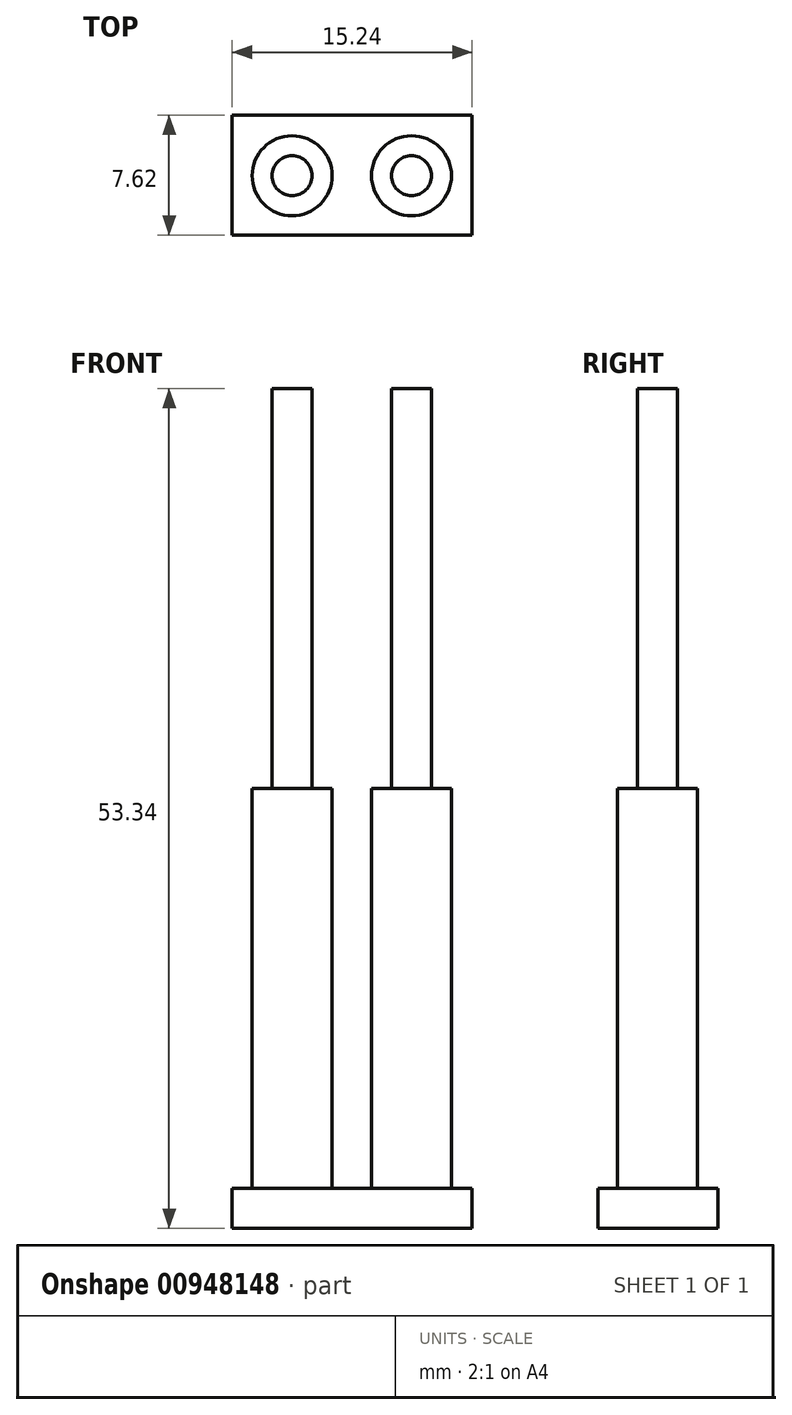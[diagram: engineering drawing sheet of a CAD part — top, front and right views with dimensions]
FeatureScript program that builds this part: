
annotation { "Feature Type Name" : "Feature", "Feature Type Description" : "" }
export const myFeature = defineFeature(function(context is Context, id is Id, definition is map)
    precondition{}
    {
        {
            var Q0;
            Q0=qCreatedBy(makeId("Top.planeOp"),FACE);
            var sketch = newSketch(context, id + "F0", { "sketchPlane" : qUnion([Q0])});
            skLineSegment(sketch, "E0.bottom", {"start": v(-47.1, -34.78) * mm, "end": v(-39.47, -34.78) * mm});
            skLineSegment(sketch, "E0.top", {"start": v(-47.1, -27.16) * mm, "end": v(-39.47, -27.16) * mm});
            skLineSegment(sketch, "E0.left", {"start": v(-47.1, -34.78) * mm, "end": v(-47.1, -27.16) * mm});
            skCircle(sketch, "E1", {"center": v(-43.28, -31) * mm, "radius": 2.54 * mm});
            skPoint(sketch, "E1.centerSnap0", {"position": v(-43.28, -27.16) * mm});
            skCircle(sketch, "E2", {"center": v(-43.28, -31) * mm, "radius": 1.27 * mm});
            skLineSegment(sketch, "E3.bottom", {"start": v(-47.1, -34.78) * mm, "end": v(-31.85, -34.78) * mm});
            skLineSegment(sketch, "E3.top", {"start": v(-47.1, -27.16) * mm, "end": v(-31.85, -27.16) * mm});
            skLineSegment(sketch, "E3.right", {"start": v(-31.85, -34.78) * mm, "end": v(-31.85, -27.16) * mm});
            skCircle(sketch, "E4", {"center": v(-35.7, -31) * mm, "radius": 2.54 * mm});
            skCircle(sketch, "E5", {"center": v(-35.7, -31) * mm, "radius": 1.27 * mm});
            skSolve(sketch);
        }
        {
            var Q0;
            Q0=makeQuery(id+"F0.imprint","IMPRINT",FACE,{"disambiguationData":[TD([[makeQuery(id+"F0.imprint","IMPRINT",EDGE,{"derivedFrom":sQuery(id+"F0.wireOp",EDGE,"E0.bottom")}),1.0]])]});
            var Q1;
            Q1=makeQuery(id+"F0.imprint","IMPRINT",FACE,{"disambiguationData":[TD([[makeQuery(id+"F0.imprint","IMPRINT",EDGE,{"derivedFrom":sQuery(id+"F0.wireOp",EDGE,"E1")}),-1.0]])]});
            var Q2;
            Q2=makeQuery(id+"F0.imprint","IMPRINT",FACE,{"disambiguationData":[TD([[makeQuery(id+"F0.imprint","IMPRINT",EDGE,{"derivedFrom":sQuery(id+"F0.wireOp",EDGE,"E1")}),1.0]])]});
            var Q3;
            Q3=makeQuery(id+"F0.imprint","IMPRINT",FACE,{"disambiguationData":[TD([[makeQuery(id+"F0.imprint","IMPRINT",EDGE,{"derivedFrom":sQuery(id+"F0.wireOp",EDGE,"E2")}),1.0]])]});
            var Q4;
            Q4=makeQuery(id+"F0.imprint","IMPRINT",FACE,{"disambiguationData":[TD([[makeQuery(id+"F0.imprint","IMPRINT",EDGE,{"derivedFrom":sQuery(id+"F0.wireOp",EDGE,"E4")}),1.0]])]});
            var Q5;
            Q5=makeQuery(id+"F0.imprint","IMPRINT",FACE,{"disambiguationData":[TD([[makeQuery(id+"F0.imprint","IMPRINT",EDGE,{"derivedFrom":sQuery(id+"F0.wireOp",EDGE,"E5")}),1.0]])]});
            extrude(context, id + "F1", {"entities" : qUnion([Q0, Q1, Q2, Q3, Q4, Q5]), "oppositeDirection" : true, "depth" : 2.54 * mm, "offsetDistance" : 25.4 * mm});
        }
        {
            var Q0;
            Q0=makeQuery(id+"F0.imprint","IMPRINT",FACE,{"disambiguationData":[TD([[makeQuery(id+"F0.imprint","IMPRINT",EDGE,{"derivedFrom":sQuery(id+"F0.wireOp",EDGE,"E1")}),1.0]])]});
            var Q1;
            Q1=makeQuery(id+"F0.imprint","IMPRINT",FACE,{"disambiguationData":[TD([[makeQuery(id+"F0.imprint","IMPRINT",EDGE,{"derivedFrom":sQuery(id+"F0.wireOp",EDGE,"E4")}),1.0]])]});
            extrude(context, id + "F2", {"entities" : qUnion([Q0, Q1]), "operationType" : NewBodyOperationType.ADD, "depth" : 25.4 * mm, "offsetDistance" : 25.4 * mm});
        }
        {
            var Q0;
            Q0=makeQuery(id+"F0.imprint","IMPRINT",FACE,{"disambiguationData":[TD([[makeQuery(id+"F0.imprint","IMPRINT",EDGE,{"derivedFrom":sQuery(id+"F0.wireOp",EDGE,"E2")}),1.0]])]});
            var Q1;
            Q1=makeQuery(id+"F0.imprint","IMPRINT",FACE,{"disambiguationData":[TD([[makeQuery(id+"F0.imprint","IMPRINT",EDGE,{"derivedFrom":sQuery(id+"F0.wireOp",EDGE,"E5")}),1.0]])]});
            extrude(context, id + "F3", {"entities" : qUnion([Q0, Q1]), "operationType" : NewBodyOperationType.ADD, "depth" : 50.8 * mm, "offsetDistance" : 25.4 * mm});
        }
    });
